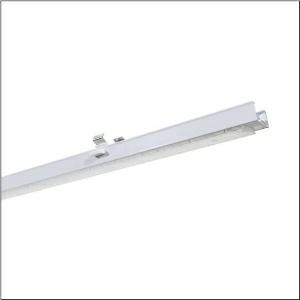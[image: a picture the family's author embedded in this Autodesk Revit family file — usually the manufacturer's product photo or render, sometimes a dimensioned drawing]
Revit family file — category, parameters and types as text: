
# Revit family: sanierungs-leuchteneinsatz_31_gen_2_51re12ma16b_3258
name_source: partatom
category: Lighting Fixtures
units: mm (PartAtom-declared; Revit-internal decimal feet)

## family parameters
Cut with Voids When Loaded = No
Host = Face
Light Source = No
Part Type = Normal
Room Calculation Point = No
Round Connector Dimension = Use Diameter
Shared = No

## types (1)
- --- (1 x LED, 6400 lm, 40 W, 3500K)
    Apparent Load = 40 VA
    CIE Flux Codes = 65 91 98 99 100
    Color Rendering = 80
    Color Temperature = 3500K
    Default Elevation = 1800 mm
    Description = Refurbishment luminaire insert Gen.2, luminaire insert, of extruded aluminium section, coated, traffic white (RAL 9016), length: 1.172mm, width: 91mm, height: 53mm, LED rated luminous flux: 6.400lm, light colour: 835, control gear: ON/OFF Multilumen, control gear: ECG Multilumen, with system connector: socket, mains connection: 220..240V, AC/DC, 0/50..60Hz, luminous flux adjustable on luminaire in four steps (3420/4540/5580/6630lm), connected load according to luminous flux setting (20/26/33/40W), primary light control with lens, of plastic, primary optical cover: cover, of PMMA, light emission: direct distribution, protection rating (complete): IP20, insulation class (complete): insulation class I (protective earthing), certification: CE, UKCA, permissible ambient temperature for indoor applications: -20..+40°C, packaging unit: 1 piece
    Height = 58 mm
    Lamp = 1 x LED
    Lamp Light Flux = 6400 lm
    Lamp Power = 40 W
    Lamp count = 1
    Length = 1172 mm
    Luminous efficacy = 160 lm/W
    Manufacturer = Siteco
    ModVariant = No
    Model = 51RE12MA16B
    Mounting Place = Ceiling
    Mounting Type = Pendant
    Number of Poles = 1
    OnlyDefault = Yes
    Power Factor = 1
    Product Name = Sanierungs-Leuchteneinsatz 31 Gen.2
    Product group = luminaire insert
    ProductGroupID = 902
    Protection Class = Protection class I
    Protection Degree = IP 20
    RLX_Detail_Level = 1
    RlxData = <blob elided: 19941 chars, md5=b9f3f8d9>
    Socket = socket
    Standby Power = 0 W
    System Light Flux = 6400 lm
    System Power = 40 W
    Type Comments = factory setting: luminous flux: 100 % | (ON | ON) | 300 mA
    Type Image = l_1266702.jpg
    URL = http://relux.com
    VarID = @adj_090925
    Voltage = 0 V
    Weight = 0.00 kg
    Width = 65 mm

## geometry (parser evidence)
native form markers: Blend x4, Sweep x11
no freeform markers — native parametric forms only
